# Revit family: Domotics-DomesticRanges-GEWISS-CHORUS_PLATES_SUPPORT_DOUBLE
name_source: partatom
category: Apparecchi elettrici
revit_build: Autodesk Revit 2016 (Build: 20161004_0715(x64)
units: mm (PartAtom-declared; Revit-internal decimal feet)

## family parameters
Basato su piano di lavoro = Sì
Condiviso = No
Mantenere orientamento annotazione = Sì
Punto di calcolo locali = No
Quota connettore circolare = Usa diametro
Sempre verticale = Sì
Taglio con vuoti quando caricato = No
Tipo di parte = Normale

## types (2) — shared parameters
Altezza foro = 45 mm  [stored 0.147638 ft]
Altezza supporto = 148 mm  [stored 0.485564 ft]
Catalogue = DOMOTICS
Catalogue Range = CHORUS - Special plates
Characteristics = Halogen free
Electrocod = 0121
Fixing = 4 screws (included)
Glow wire test: = 650 °C
IDF = bda46bbc-e72c-478e-a126-6b411c62c67b
IDT = 60e3146f-c8da-42a8-b8a7-65fd8c53e3a3
Immagine tipo = GW16812.jpg
Larghezza foro = 138 mm  [stored 0.452756 ft]
Larghezza supporto = 184 mm  [stored 0.603675 ft]
Materiale supporto = GEWISS - ACCIAIO SUPPORTO
Produttore = GEWISS S.p.A.
Prospetto di default = 1219 mm
SEO = Support
Standard; = EN 60669-1
Technical sheet = https://www.gewiss.com
Thermo-pressure with ball = 70
URL = https://www.gewiss.com
Version file RFA = 18.0

## per-type parameters (varying)
| type | Description: | Descrizione | EAN code | For box | Modello |
| GW16808 - 4+4P | 4+4 gang | SUPPORT, ITALIAN STANDARD, 8-GANG | 8011564274815 | 8 modules | GW16808 |
| GW16812 - 6+6P | 6+6 gang | SUPPORT, ITALIAN STANDARD, 12-GANG | 8011564274822 | 12 modules | GW16812 |

note: source unit labels omitted for Thermo-pressure with ball — the stored unit's dimension contradicts the parameter name (converter mislabeling)

note: [stored X ft] marks values corroborated as IEEE doubles in the binary element streams (Revit-internal decimal feet)
